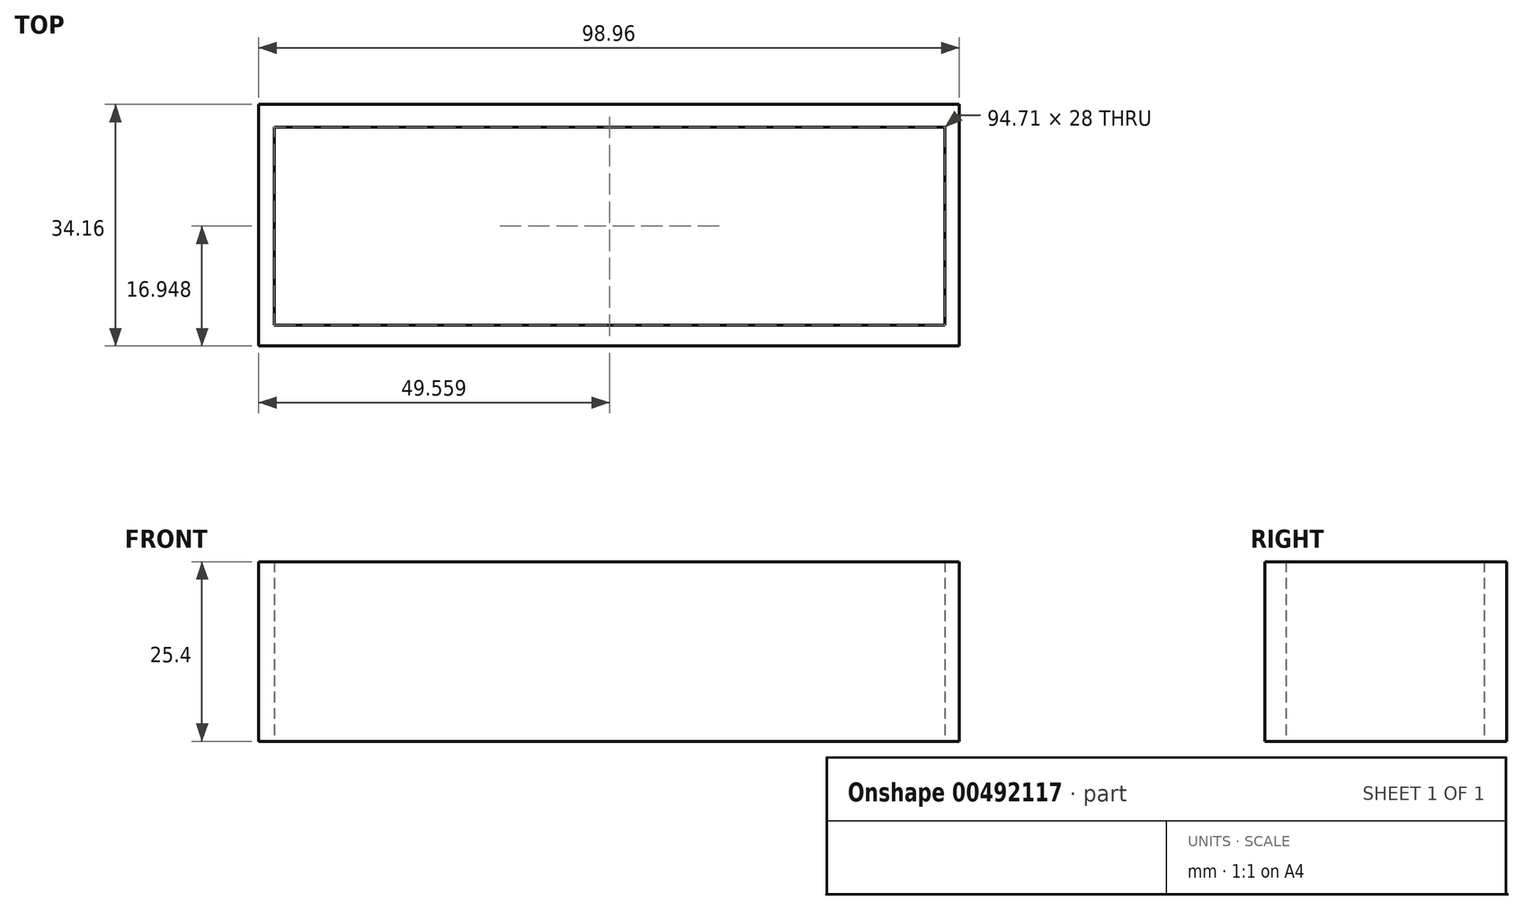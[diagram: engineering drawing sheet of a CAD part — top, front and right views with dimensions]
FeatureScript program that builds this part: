
annotation { "Feature Type Name" : "Feature", "Feature Type Description" : "" }
export const myFeature = defineFeature(function(context is Context, id is Id, definition is map)
    precondition{}
    {
        {
            var Q0;
            Q0=qCreatedBy(makeId("Top.planeOp"),FACE);
            var sketch = newSketch(context, id + "F0", { "sketchPlane" : qUnion([Q0])});
            skLineSegment(sketch, "E0.bottom", {"start": v(-76.49, 19.07) * mm, "end": v(22.47, 19.07) * mm});
            skLineSegment(sketch, "E0.top", {"start": v(-76.49, -15.1) * mm, "end": v(22.47, -15.1) * mm});
            skLineSegment(sketch, "E0.left", {"start": v(-76.49, 19.07) * mm, "end": v(-76.49, -15.1) * mm});
            skLineSegment(sketch, "E0.right", {"start": v(22.47, 19.07) * mm, "end": v(22.47, -15.1) * mm});
            skLineSegment(sketch, "E1.bottom", {"start": v(-74.29, 15.86) * mm, "end": v(20.43, 15.86) * mm});
            skLineSegment(sketch, "E1.top", {"start": v(-74.29, -12.14) * mm, "end": v(20.43, -12.14) * mm});
            skLineSegment(sketch, "E1.left", {"start": v(-74.29, 15.86) * mm, "end": v(-74.29, -12.14) * mm});
            skLineSegment(sketch, "E1.right", {"start": v(20.43, 15.86) * mm, "end": v(20.43, -12.14) * mm});
            skSolve(sketch);
        }
        {
            var Q0;
            Q0 = qSketchRegion(id + "F0", true);
            var Q1;
            Q1 = qSketchRegion(id + "F4EHppPOZxjmO62_0", true);
            extrude(context, id + "F1", {"entities" : qUnion([Q0, Q1]), "depth" : 25.4 * mm});
        }
    });
